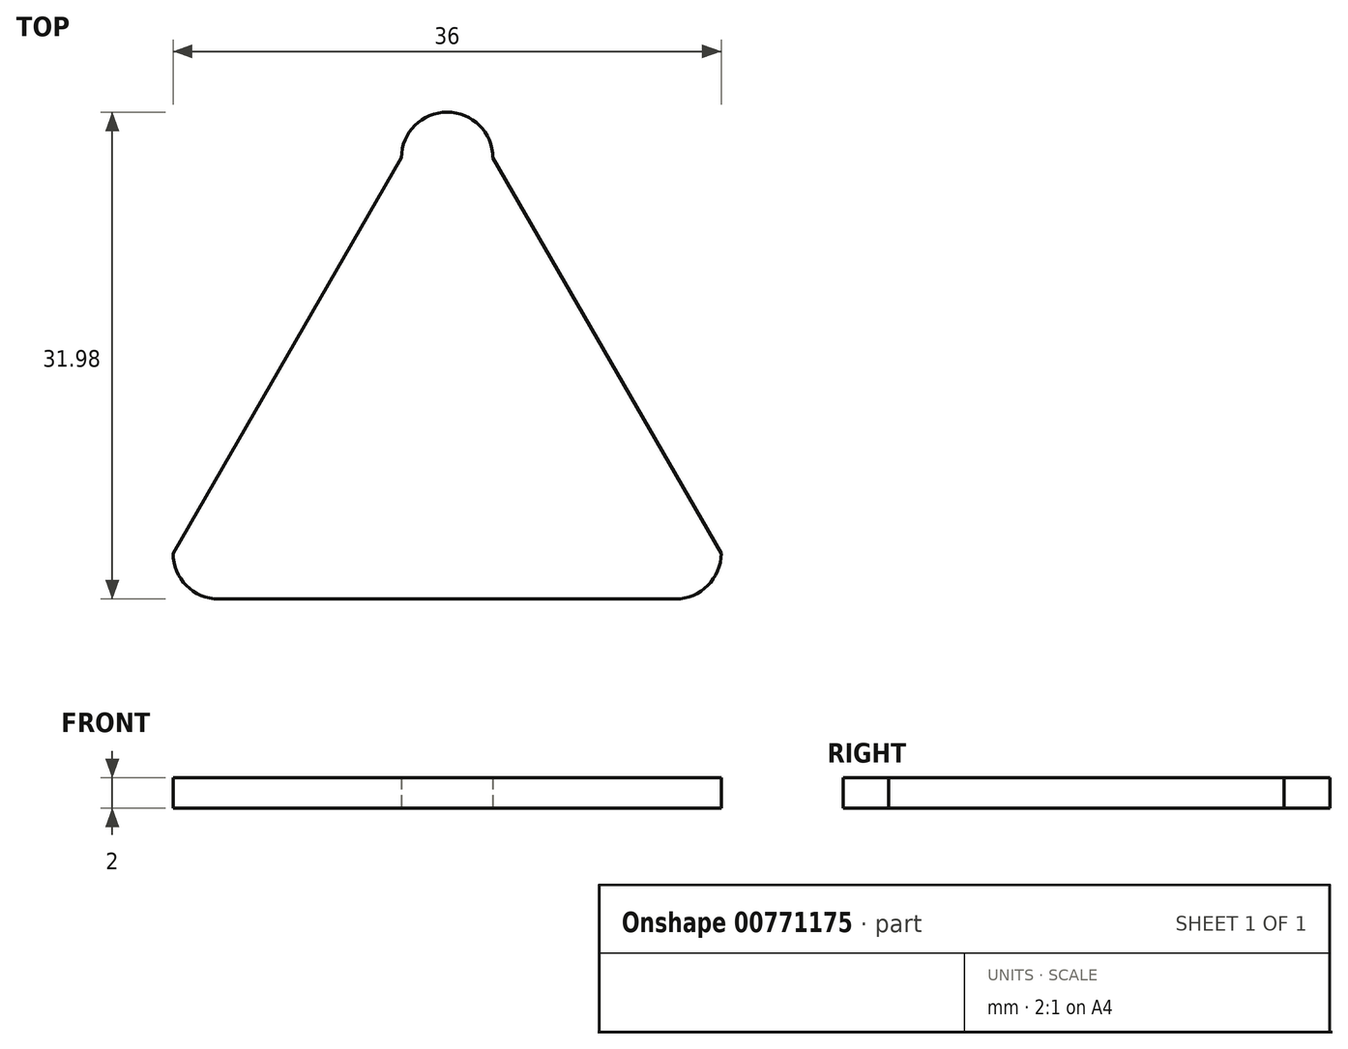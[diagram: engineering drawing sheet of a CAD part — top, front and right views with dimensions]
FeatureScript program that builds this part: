
annotation { "Feature Type Name" : "Feature", "Feature Type Description" : "" }
export const myFeature = defineFeature(function(context is Context, id is Id, definition is map)
    precondition{}
    {
        {
            var Q0;
            Q0=qCreatedBy(makeId("Top.planeOp"),FACE);
            var sketch = newSketch(context, id + "F0", { "sketchPlane" : qUnion([Q0])});
            skLineSegment(sketch, "E0", {"start": v(0, 0) * mm, "end": v(-30, 0) * mm});
            skArc(sketch, "E1", {"start": v(-33, 3) * mm, "mid": v(-32.12, 0.88) * mm, "end": v(-30, 0) * mm});
            skArc(sketch, "E2", {"start": v(0, 0) * mm, "mid": v(2.12, 0.88) * mm, "end": v(3, 3) * mm});
            skLineSegment(sketch, "E3", {"start": v(-33, 3) * mm, "end": v(-18, 28.98) * mm});
            skLineSegment(sketch, "E4", {"start": v(3, 3) * mm, "end": v(-12, 28.98) * mm});
            skArc(sketch, "E5", {"start": v(-12, 28.98) * mm, "mid": v(-15, 31.98) * mm, "end": v(-18, 28.98) * mm});
            skSolve(sketch);
        }
        {
            var Q0;
            Q0 = qSketchRegion(id + "F0", true);
            extrude(context, id + "F1", {"entities" : qUnion([Q0]), "depth" : 2 * mm, "offsetDistance" : 25 * mm});
        }
    });
